# Revit family: Vario-DP_axiální_DN015_RFA_2019
name_source: partatom
category: Pipe Accessories
units: mm (PartAtom-declared; Revit-internal decimal feet)

## family parameters
Always vertical = Yes
Cut with Voids When Loaded = No
Part Type = Valve - Breaks Into
Round Connector Dimension = Use Diameter
Shared = No
Work Plane-Based = No

## types (1)
- Vario-DP, axiální, DN15
    BBVIS = No
    BY = 16 mm  [stored 0.0524934 ft]
    BZ = 18 mm  [stored 0.0590551 ft]
    C = 3 mm  [stored 0.00984252 ft]
    CAT = No
    CAT0 = Yes
    CenSd_RT1_6 = 11 mm  [stored 0.0360892 ft]
    CenSd_RT22_6 = 15 mm  [stored 0.0492126 ft]
    D = 15 mm
    DS1 = 15 mm  [stored 0.0492126 ft]
    DS2 = 9 mm  [stored 0.0295276 ft]
    DS3 = 4 mm  [stored 0.0131234 ft]
    DT = 21 mm  [stored 0.0688976 ft]
    Description = Termostatický radiátorový ventil s omezovačem max. průtoku; DN15; rozsah nastavení omezovače max. průtok: 20-340l/h
    E = 26 mm  [stored 0.0853018 ft]
    ENBL350 = No
    H = 23 mm  [stored 0.0754593 ft]
    HS = 16 mm  [stored 0.0524934 ft]
    HS__ve = -16 mm  [stored -0.0524934 ft]
    L = 45 mm
    L1 = 8 mm  [stored 0.0262467 ft]
    L1__ve = -8 mm  [stored -0.0262467 ft]
    L2 = 13 mm  [stored 0.0426509 ft]
    L2D = 45 mm
    L2D_Min = 30 mm  [stored 0.0984252 ft]
    L2__ve = -13 mm  [stored -0.0426509 ft]
    LD = 58 mm  [stored 0.190289 ft]
    LLDAndHLD = Yes
    LLDONLY = Yes
    LP = 11 mm  [stored 0.0360892 ft]
    L_ = 45 mm
    MC Enable LOD 200 = No
    MC Enable LOD 350 = No
    MC Pressure Drop Maximum Value = 0.0 Pa
    MC Pressure Drop Minimum Value = 0.0 Pa
    MC Product Code = VARIO-DP; axiální  DN15; (obj.č.: 163020100); dpmin=15kPa; dpmax: 70kPa;; rozsah nastavení 20-340l/h
    MC Throttling Maximum Value = 0
    MC Throttling Minimum Value = 0
    MC Use Limits From Balancing Method = No
    Manufacturer = Hydronix
    QmdConnectorList = 301;D;302;D
    RR = 5 mm  [stored 0.0164042 ft]
    RT = 11 mm  [stored 0.0360892 ft]
    RT0 = 10 mm  [stored 0.0328084 ft]
    RT02 = 16 mm  [stored 0.0524934 ft]
    RT1 = 13 mm  [stored 0.0426509 ft]
    RT2 = 11 mm  [stored 0.0360892 ft]
    RT22 = 18 mm  [stored 0.0590551 ft]
    RT4 = 11 mm  [stored 0.0360892 ft]
    RT_1 = 11 mm  [stored 0.0360892 ft]
    TL = 13 mm  [stored 0.0426509 ft]
    TL__ve = -13 mm  [stored -0.0426509 ft]
    Type Comments = Termostatický radiátorový ventil s integrovaným omezovačem průtoku; axiální; závitový, PN10; +0~+90°C; pracovní dp 15-70kPa; max. síla pohonu 120N; připojení hlavice: M30x1,5
    URL = www.hydronix.cz
    VIS0 = No
    W2D = 15 mm  [stored 0.0492126 ft]
    Z1 = 5 mm  [stored 0.0164042 ft]
    Z1__ve = -5 mm  [stored -0.0164042 ft]
    magiPartTypeId = 303
    magiProductFamilyId = 9b3b607f8b78467aae107e3a56a735
    magiProductId = f04308fc8aa540afac1dfaa22e7090

note: [stored X ft] marks values corroborated as IEEE doubles in the binary element streams (Revit-internal decimal feet)

## geometry (parser evidence)
native form markers: Sweep x14
no freeform markers — native parametric forms only
